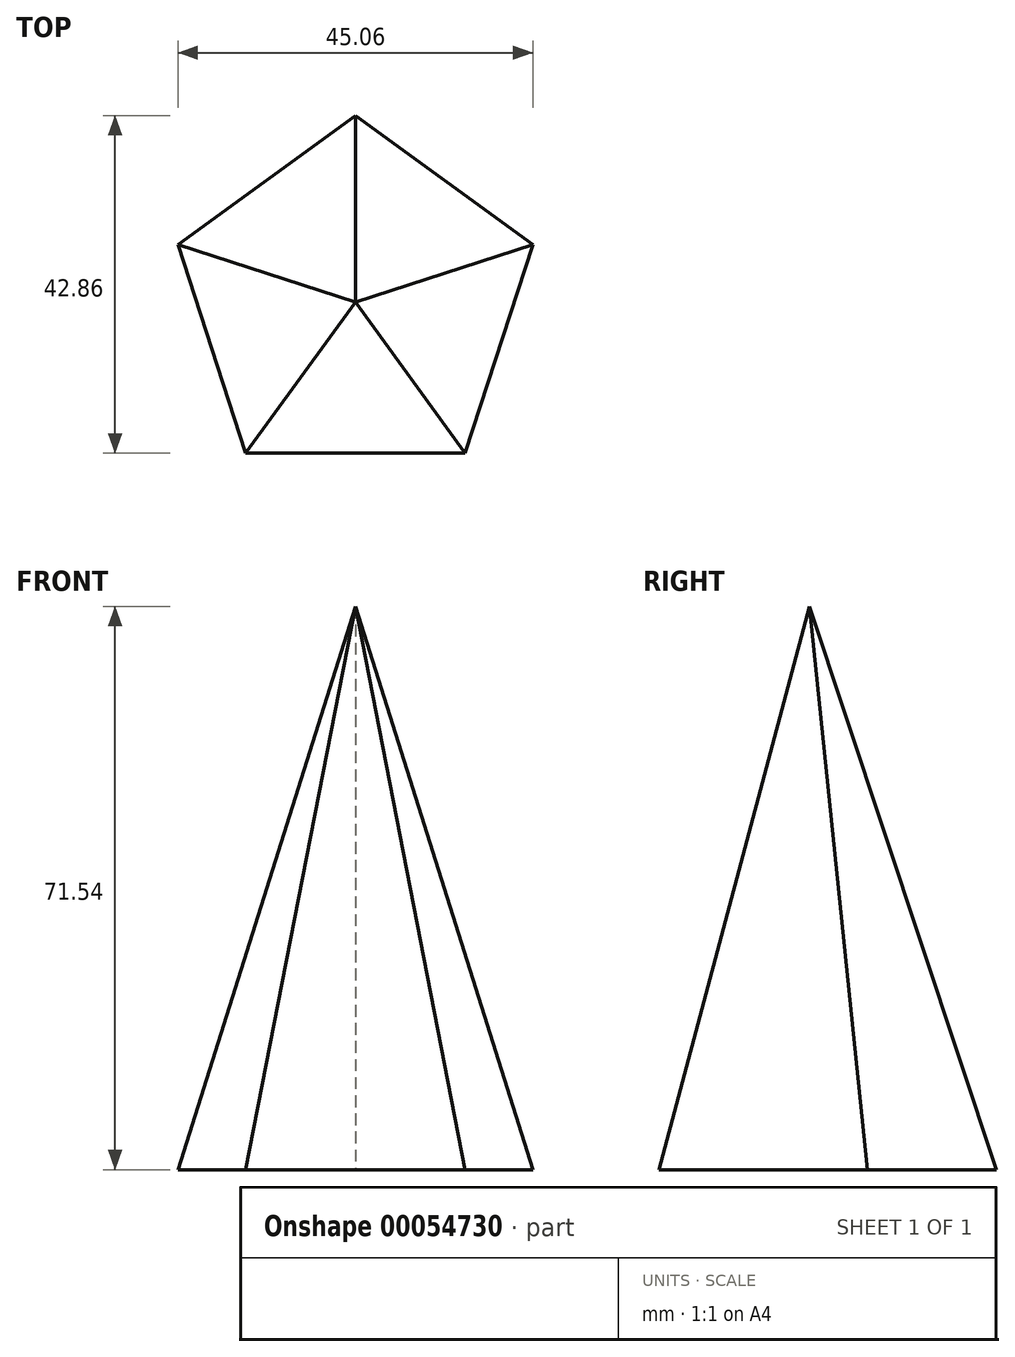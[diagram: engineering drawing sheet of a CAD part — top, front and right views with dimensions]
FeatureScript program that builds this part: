
annotation { "Feature Type Name" : "Feature", "Feature Type Description" : "" }
export const myFeature = defineFeature(function(context is Context, id is Id, definition is map)
    precondition{}
    {
        {
            var Q0;
            Q0=qCreatedBy(makeId("Top.planeOp"),FACE);
            var sketch = newSketch(context, id + "F0", { "sketchPlane" : qUnion([Q0])});
            skCircle(sketch, "E0.cCircle", {"center": v(0, 0) * mm, "radius": 19.17 * mm, "construction": true});
            skLineSegment(sketch, "E0.0", {"start": v(22.53, 7.32) * mm, "end": v(13.93, -19.17) * mm});
            skLineSegment(sketch, "E0.1", {"start": v(13.93, -19.17) * mm, "end": v(-13.93, -19.17) * mm});
            skLineSegment(sketch, "E0.2", {"start": v(-13.93, -19.17) * mm, "end": v(-22.53, 7.32) * mm});
            skLineSegment(sketch, "E0.3", {"start": v(-22.53, 7.32) * mm, "end": v(0, 23.7) * mm});
            skLineSegment(sketch, "E0.4", {"start": v(0, 23.7) * mm, "end": v(22.53, 7.32) * mm});
            skPoint(sketch, "E0.0.midPoint", {"position": v(18.23, -5.92) * mm});
            skSolve(sketch);
        }
        {
            var Q0;
            Q0=makeQuery(id+"F0.imprint","IMPRINT",FACE,{"disambiguationData":[TD([[makeQuery(id+"F0.imprint","IMPRINT",EDGE,{"derivedFrom":sQuery(id+"F0.wireOp",EDGE,"E0.0")}),-1.0]])]});
            extrude(context, id + "F1", {"entities" : qUnion([Q0]), "depth" : 73 * mm, "hasDraft" : true, "draftAngle" : 15 * degree, "draftPullDirection" : true});
        }
    });
